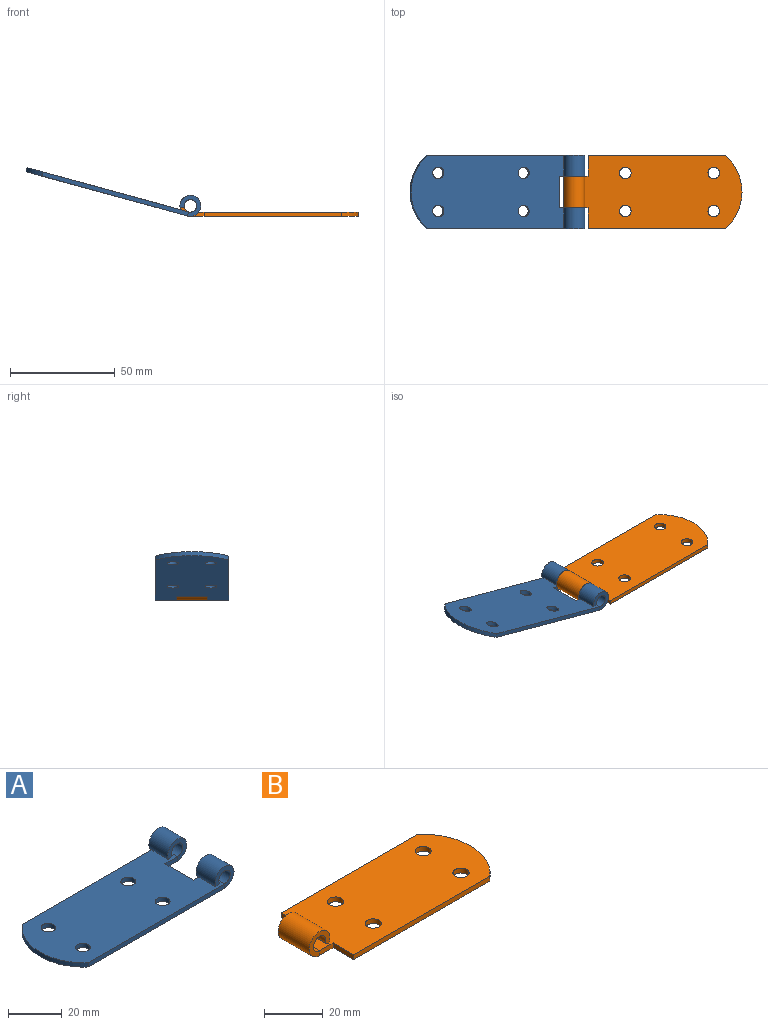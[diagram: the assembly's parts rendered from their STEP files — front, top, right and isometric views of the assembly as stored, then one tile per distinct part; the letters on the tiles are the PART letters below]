
ASSEMBLY  parts=2 mates=1
PART A: 22 faces, bbox 85x35x10 mm
  f0: plane 10x10mm, normal (0,1,0), area 41.2mm2, adj f1,f3,f4,f14
  f1: plane 10x1.81mm, normal (0.42,0,-0.91), area 20mm2, adj f0,f2,f3,f4
  f2: plane 10x10mm, normal (0,-1,0), area 41.2mm2, adj f1,f3,f4,f19
  f3: cylinder r=5mm len=10mm, axis (0,-1,0), area 257.5mm2, adj f0,f1,f2,f20
  f4: cylinder r=3mm len=10mm, axis (0,-1,0), area 154.5mm2, adj f0,f1,f2,f21
  f5: plane 10x10mm, normal (0,-1,0), area 41.2mm2, adj f7,f8,f9,f12
  f6: plane 10x10mm, normal (0,1,0), area 41.2mm2, adj f7,f8,f9,f11
  f7: plane 10x1.81mm, normal (0.42,0,-0.91), area 20mm2, adj f5,f6,f8,f9
  f8: cylinder r=5mm len=10mm, axis (0,-1,0), area 257.5mm2, adj f5,f6,f7,f20
  f9: cylinder r=3mm len=10mm, axis (0,-1,0), area 154.5mm2, adj f5,f6,f7,f21
  f10: plane 15x2mm, normal (1,0,0), area 30mm2, adj f11,f19,f20,f21
  f11: plane 6.5x2mm, normal (0,1,0), area 13mm2, adj f6,f10,f20,f21
  f12: plane 72x2mm, normal (0,-1,0), area 144mm2, adj f5,f13,f20,f21
  f13: cylinder r=23.14mm len=35mm, axis (0,0,-1), area 79.4mm2, adj f12,f14,f20,f21
  f14: plane 72x2mm, normal (0,1,0), area 144mm2, adj f0,f13,f20,f21
  f15: cylinder r=2.75mm len=5.5mm, axis (0,0,-1), area 34.6mm2, adj f20,f21
  f16: cylinder r=2.75mm len=5.5mm, axis (0,0,-1), area 34.6mm2, adj f20,f21
  f17: cylinder r=2.75mm len=5.5mm, axis (0,0,-1), area 34.6mm2, adj f20,f21
  f18: cylinder r=2.75mm len=5.5mm, axis (0,0,-1), area 34.6mm2, adj f20,f21
  f19: plane 6.5x2mm, normal (0,-1,0), area 13mm2, adj f2,f10,f20,f21
  f20: plane 80x35mm, normal (0,0,-1), area 2521.7mm2, adj f3,f8,f10,f11,f12,f13,f14,f15
  f21: plane 80x35mm, normal (0,0,1), area 2521.7mm2, adj f4,f9,f10,f11,f12,f13,f14,f15
PART B: 18 faces, bbox 85x35x10 mm
  f0: plane 10x10mm, normal (0,-1,0), area 41.2mm2, adj f1,f3,f4,f9
  f1: plane 15x1.81mm, normal (-0.42,0,-0.91), area 30mm2, adj f0,f2,f3,f4
  f2: plane 10x10mm, normal (0,1,0), area 41.2mm2, adj f1,f3,f4,f10
  f3: cylinder r=5mm len=15mm, axis (0,-1,0), area 386.3mm2, adj f0,f1,f2,f16
  f4: cylinder r=3mm len=15mm, axis (0,-1,0), area 231.8mm2, adj f0,f1,f2,f17
  f5: plane 65.5x2mm, normal (0,1,0), area 131mm2, adj f6,f15,f16,f17
  f6: cylinder r=23.14mm len=35mm, axis (0,0,-1), area 79.4mm2, adj f5,f7,f16,f17
  f7: plane 65.5x2mm, normal (0,-1,0), area 131mm2, adj f6,f8,f16,f17
  f8: plane 10x2mm, normal (-1,0,0), area 20mm2, adj f7,f9,f16,f17
  f9: plane 6.5x2mm, normal (0,-1,0), area 13mm2, adj f0,f8,f16,f17
  f10: plane 6.5x2mm, normal (0,1,0), area 13mm2, adj f2,f15,f16,f17
  f11: cylinder r=2.75mm len=5.5mm, axis (0,0,-1), area 34.6mm2, adj f16,f17
  f12: cylinder r=2.75mm len=5.5mm, axis (0,0,-1), area 34.6mm2, adj f16,f17
  f13: cylinder r=2.75mm len=5.5mm, axis (0,0,-1), area 34.6mm2, adj f16,f17
  f14: cylinder r=2.75mm len=5.5mm, axis (0,0,-1), area 34.6mm2, adj f16,f17
  f15: plane 10x2mm, normal (-1,0,0), area 20mm2, adj f5,f10,f16,f17
  f16: plane 80x35mm, normal (0,0,-1), area 2489.2mm2, adj f3,f5,f6,f7,f8,f9,f10,f11
  f17: plane 80x35mm, normal (0,0,1), area 2489.2mm2, adj f4,f5,f6,f7,f8,f9,f10,f11
PLACE A rot(axis=(0,1,0),15.3deg) t=(-13.34,2.6,15.44)mm
PLACE B t=(-13.34,2.6,15.44)mm fixed
MATE revolute B.f3 <-> A.f3  axis (0,-1,0) through (-13.34,-4.9,15.44)mm
